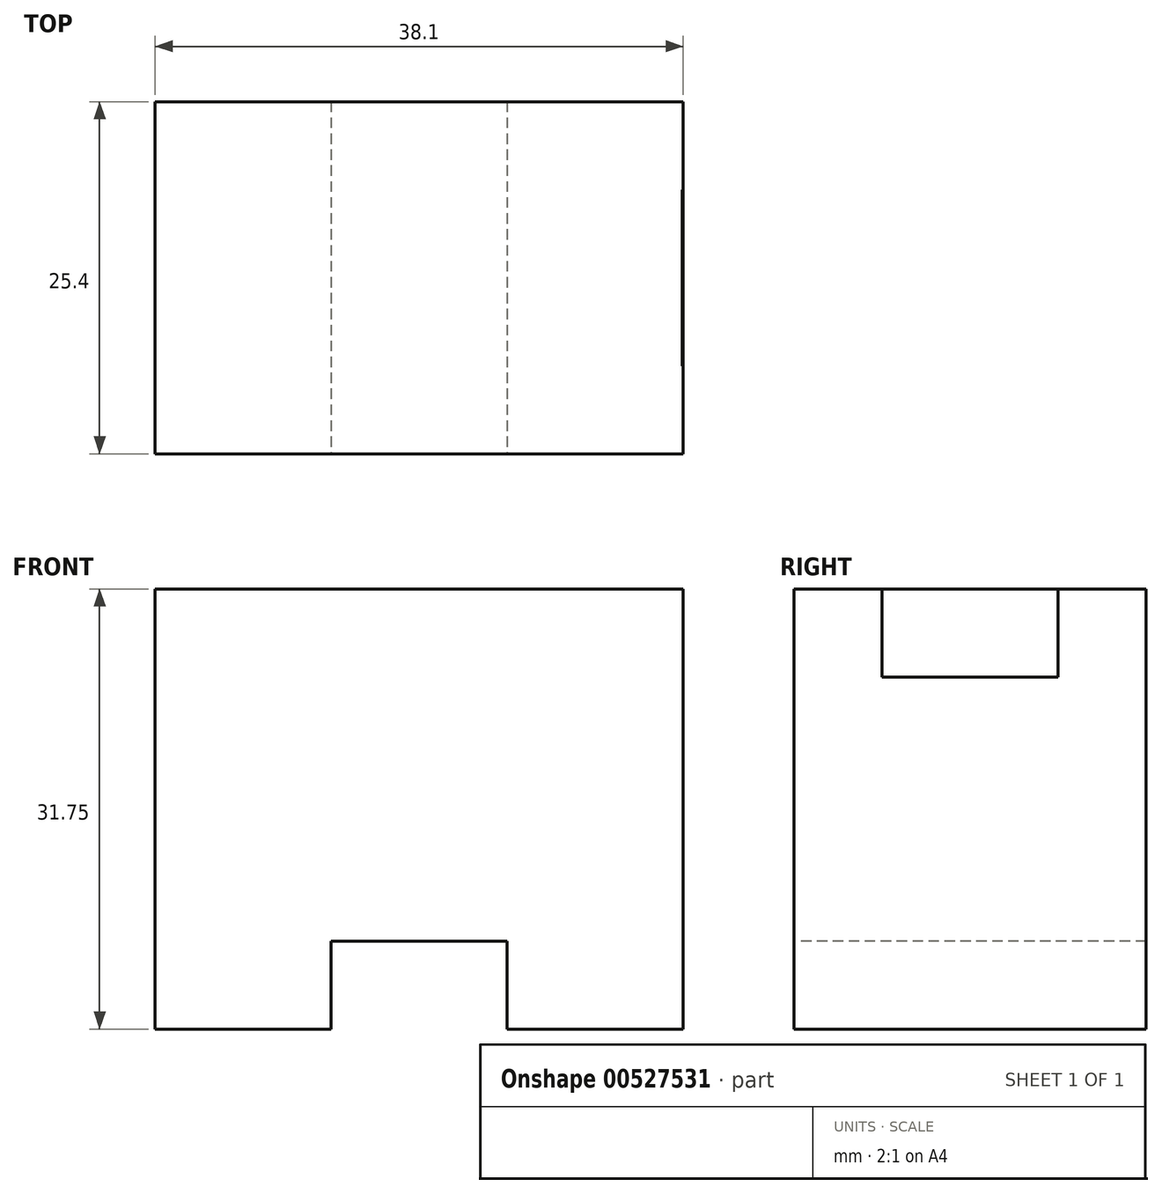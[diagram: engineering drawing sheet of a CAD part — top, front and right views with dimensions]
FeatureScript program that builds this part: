
annotation { "Feature Type Name" : "Feature", "Feature Type Description" : "" }
export const myFeature = defineFeature(function(context is Context, id is Id, definition is map)
    precondition{}
    {
        {
            var Q0;
            Q0=qCreatedBy(makeId("Front.planeOp"),FACE);
            var sketch = newSketch(context, id + "F0", { "sketchPlane" : qUnion([Q0])});
            skLineSegment(sketch, "E0", {"start": v(0, 0) * mm, "end": v(38.1, 0) * mm});
            skLineSegment(sketch, "E1", {"start": v(38.1, 0) * mm, "end": v(38.1, 31.75) * mm});
            skLineSegment(sketch, "E2", {"start": v(38.1, 31.75) * mm, "end": v(0, 31.75) * mm});
            skLineSegment(sketch, "E3", {"start": v(0, 31.75) * mm, "end": v(0, 0) * mm});
            skSolve(sketch);
        }
        {
            var Q0;
            Q0 = qSketchRegion(id + "F0", true);
            extrude(context, id + "F1", {"entities" : qUnion([Q0]), "depth" : 25.4 * mm, "offsetDistance" : 25.4 * mm});
        }
        {
            var Q0;
            Q0=makeQuery(id+"F1.opExtrude","CAP_FACE",FACE,{"disambiguationData":[OSD([sQuery(id+"F0.wireOp",EDGE,"E0"),sQuery(id+"F0.wireOp",EDGE,"E1"),sQuery(id+"F0.wireOp",EDGE,"E2"),sQuery(id+"F0.wireOp",EDGE,"E3")])],"isStart":false});
            var sketch = newSketch(context, id + "F2", { "sketchPlane" : qUnion([Q0])});
            skLineSegment(sketch, "E4", {"start": v(12.7, 0) * mm, "end": v(12.7, 6.35) * mm});
            skLineSegment(sketch, "E5", {"start": v(12.7, 6.35) * mm, "end": v(25.4, 6.35) * mm});
            skLineSegment(sketch, "E6", {"start": v(25.4, 6.35) * mm, "end": v(25.4, 0) * mm});
            skLineSegment(sketch, "E7", {"start": v(12.7, 0) * mm, "end": v(0, 0) * mm});
            skLineSegment(sketch, "E8", {"start": v(25.4, 0) * mm, "end": v(38.1, 0) * mm});
            skSolve(sketch);
        }
        {
            var Q0;
            Q0 = qSketchRegion(id + "F2", true);
            var Q1;
            {var subQ0=sQuery(id+"F2.wireOp",EDGE,"E4");Q1=makeQuery(id+"F2.imprint","IMPRINT",FACE,{"disambiguationData":[TD([[makeQuery(id+"F2.imprint","IMPRINT",EDGE,{"derivedFrom":subQ0}),-1.0]])]});}
            extrude(context, id + "F3", {"entities" : qUnion([Q0, Q1]), "operationType" : NewBodyOperationType.REMOVE, "oppositeDirection" : true, "depth" : 25.4 * mm, "offsetDistance" : 25.4 * mm});
        }
        {
            var Q0;
            Q0=makeQuery(id+"F1.opExtrude","SWEPT_FACE",FACE,{"disambiguationData":[OSD([sQuery(id+"F0.wireOp",EDGE,"E1")])]});
            var sketch = newSketch(context, id + "F4", { "sketchPlane" : qUnion([Q0])});
            skLineSegment(sketch, "E9", {"start": v(0, 31.75) * mm, "end": v(-6.35, 31.75) * mm});
            skLineSegment(sketch, "E10", {"start": v(-6.35, 31.75) * mm, "end": v(-6.35, 25.4) * mm});
            skLineSegment(sketch, "E11", {"start": v(-6.35, 25.4) * mm, "end": v(-19.05, 25.4) * mm});
            skLineSegment(sketch, "E12", {"start": v(-19.05, 25.4) * mm, "end": v(-19.05, 31.75) * mm});
            skLineSegment(sketch, "E13", {"start": v(-19.05, 31.75) * mm, "end": v(-25.4, 31.75) * mm});
            skSolve(sketch);
        }
        {
            var Q0;
            Q0 = qSketchRegion(id + "F4", true);
            var Q1;
            {var subQ0=sQuery(id+"F4.wireOp",EDGE,"E10");Q1=makeQuery(id+"F4.imprint","IMPRINT",FACE,{"disambiguationData":[TD([[makeQuery(id+"F4.imprint","IMPRINT",EDGE,{"derivedFrom":subQ0}),-1.0]])]});}
            extrude(context, id + "F5", {"entities" : qUnion([Q0, Q1]), "operationType" : NewBodyOperationType.REMOVE, "oppositeDirection" : true, "depth" : 6 / 101.6 * mm, "offsetDistance" : 25.4 * mm});
        }
    });
